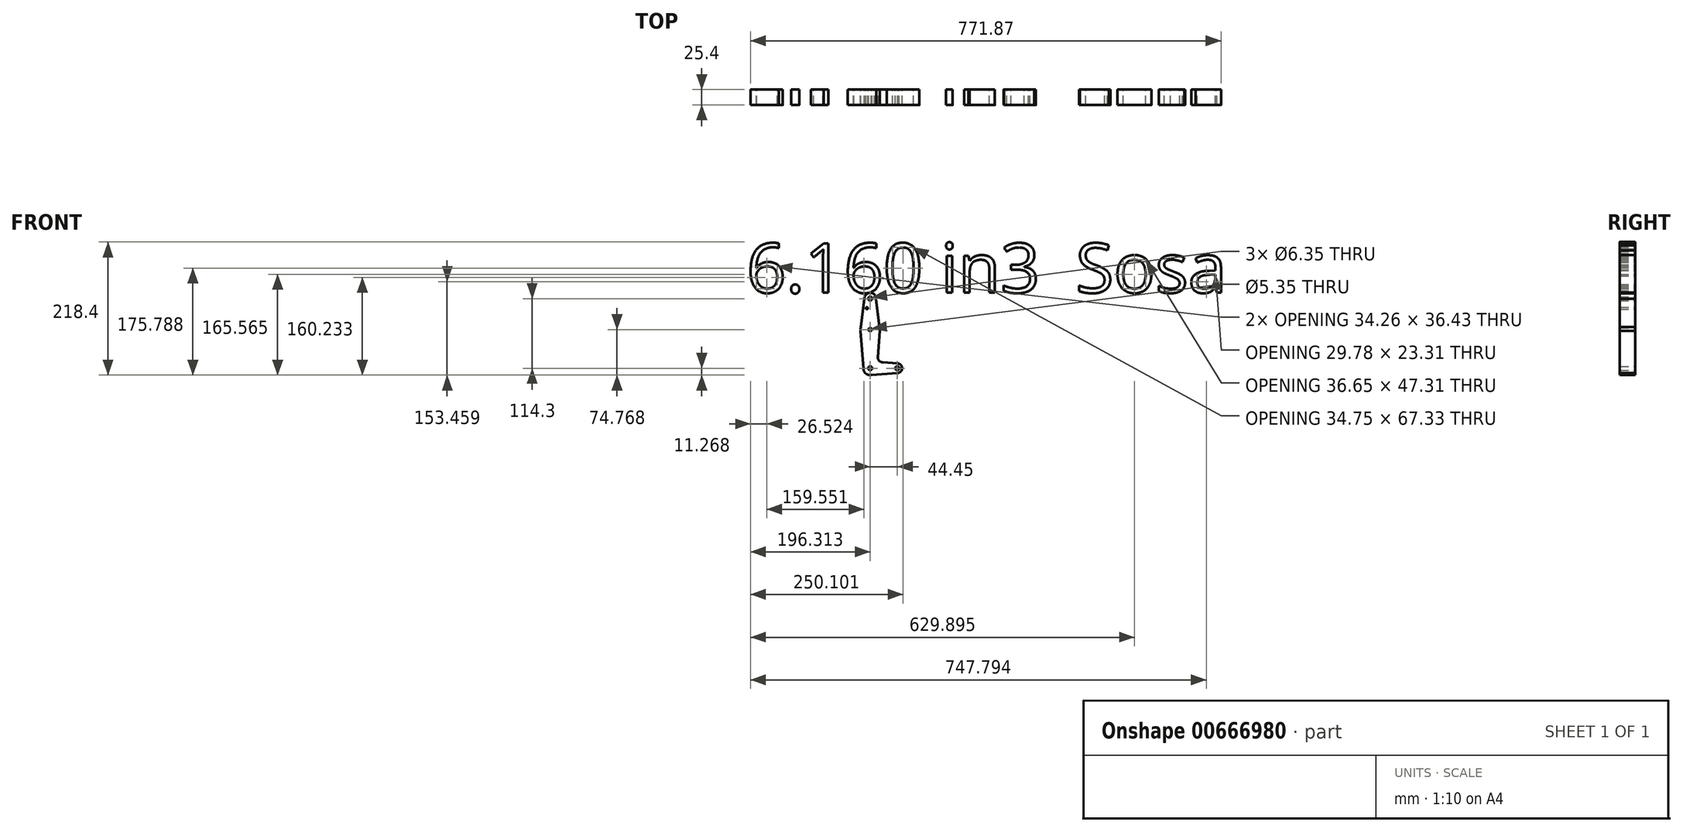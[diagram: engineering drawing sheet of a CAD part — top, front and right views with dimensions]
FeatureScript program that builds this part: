
annotation { "Feature Type Name" : "Feature", "Feature Type Description" : "" }
export const myFeature = defineFeature(function(context is Context, id is Id, definition is map)
    precondition{}
    {
        {
            var Q0;
            Q0=qCreatedBy(makeId("Front.planeOp"),FACE);
            var sketch = newSketch(context, id + "F0", { "sketchPlane" : qUnion([Q0])});
            skLineSegment(sketch, "E0", {"start": v(-391.22, 176.18) * mm, "end": v(-391.22, 61.88) * mm});
            skCircle(sketch, "E1", {"center": v(-391.22, 176.18) * mm, "radius": 9.53 * mm});
            skCircle(sketch, "E2", {"center": v(-391.22, 125.38) * mm, "radius": 15.88 * mm});
            skPoint(sketch, "E3.trimOffspring.end.orphan", {"position": v(-407.93, 125.38) * mm});
            skLineSegment(sketch, "E4", {"start": v(-375.46, 123.45) * mm, "end": v(-375.48, 123.31) * mm});
            skPoint(sketch, "E5.orphan", {"position": v(-391.22, 54) * mm});
            skPoint(sketch, "E6.center.orphan", {"position": v(-346.77, 61.88) * mm});
            skArc(sketch, "E7", {"start": v(-347.66, 54) * mm, "mid": v(-346.77, 53.94) * mm, "end": v(-345.87, 54) * mm});
            skLineSegment(sketch, "E8", {"start": v(-391.22, 61.88) * mm, "end": v(-346.77, 61.88) * mm});
            skCircle(sketch, "E9", {"center": v(-346.77, 61.88) * mm, "radius": 7.94 * mm});
            skCircle(sketch, "E10", {"center": v(-391.22, 61.88) * mm, "radius": 11.27 * mm});
            skLineSegment(sketch, "E11", {"start": v(-375.48, 123.31) * mm, "end": v(-378.6, 80.16) * mm});
            skLineSegment(sketch, "E12", {"start": v(-391.22, 50.61) * mm, "end": v(-345.87, 54) * mm});
            skLineSegment(sketch, "E13", {"start": v(-371.26, 71.66) * mm, "end": v(-345.87, 69.77) * mm});
            skPoint(sketch, "E14.end.orphan", {"position": v(-402.52, 61.88) * mm});
            skPoint(sketch, "E15.start.orphan", {"position": v(-400.74, 176.18) * mm});
            skLineSegment(sketch, "E16", {"start": v(-400.74, 176.18) * mm, "end": v(-407.1, 125.38) * mm});
            skLineSegment(sketch, "E17", {"start": v(-407.1, 125.38) * mm, "end": v(-402.45, 61.07) * mm});
            skPoint(sketch, "E18.orphan", {"position": v(-381.65, 176.18) * mm});
            skPoint(sketch, "E19.orphan", {"position": v(-375.22, 125.38) * mm});
            skLineSegment(sketch, "E20", {"start": v(-375.82, 129.26) * mm, "end": v(-375.34, 125.38) * mm});
            skLineSegment(sketch, "E21", {"start": v(-381.7, 176.19) * mm, "end": v(-375.34, 125.38) * mm});
            skCircle(sketch, "E22", {"center": v(-391.22, 176.18) * mm, "radius": 3.18 * mm});
            skCircle(sketch, "E23", {"center": v(-396.57, 160.4) * mm, "radius": 1.59 * mm});
            skCircle(sketch, "E24", {"center": v(-391.22, 125.38) * mm, "radius": 2.67 * mm});
            skCircle(sketch, "E25", {"center": v(-391.22, 61.88) * mm, "radius": 3.18 * mm});
            skCircle(sketch, "E26", {"center": v(-346.77, 61.88) * mm, "radius": 3.18 * mm});
            skArc(sketch, "E27.filletArc", {"start": v(-378.6, 80.16) * mm, "mid": v(-376.69, 74.4) * mm, "end": v(-371.26, 71.66) * mm});
            skText(sketch, "E28", { "text": "6.160 in3  Sosa", "fontName": "OpenSans-Regular.ttf"});
            const initialGuessF0  = {"E28": [-0.594, 0.18594, 1, 0, 0.0815]};
            skSetInitialGuess(sketch, initialGuessF0);
            skSolve(sketch);
        }
        {
            var Q0;
            Q0 = qSketchRegion(id + "F0", true);
            var Q1;
            {var subQ0=sQuery(id+"F0.wireOp",EDGE,"E10");var subQ1=sQuery(id+"F0.wireOp",EDGE,"E0");var subQ2=makeQuery(id+"F0.imprint","INTERSECT",VERTEX,{"derivedFrom":[subQ1,subQ0]});Q1=makeQuery(id+"F0.imprint","IMPRINT",FACE,{"disambiguationData":[TD([[makeQuery(id+"F0.imprint","IMPRINT",EDGE,{"disambiguationData":[TD([[subQ2,-1.0]])],"derivedFrom":subQ1}),1.0]])]});}
            extrude(context, id + "F1", {"entities" : qUnion([Q0, Q1]), "depth" : 25.4 * mm, "offsetDistance" : 25.4 * mm});
        }
    });
